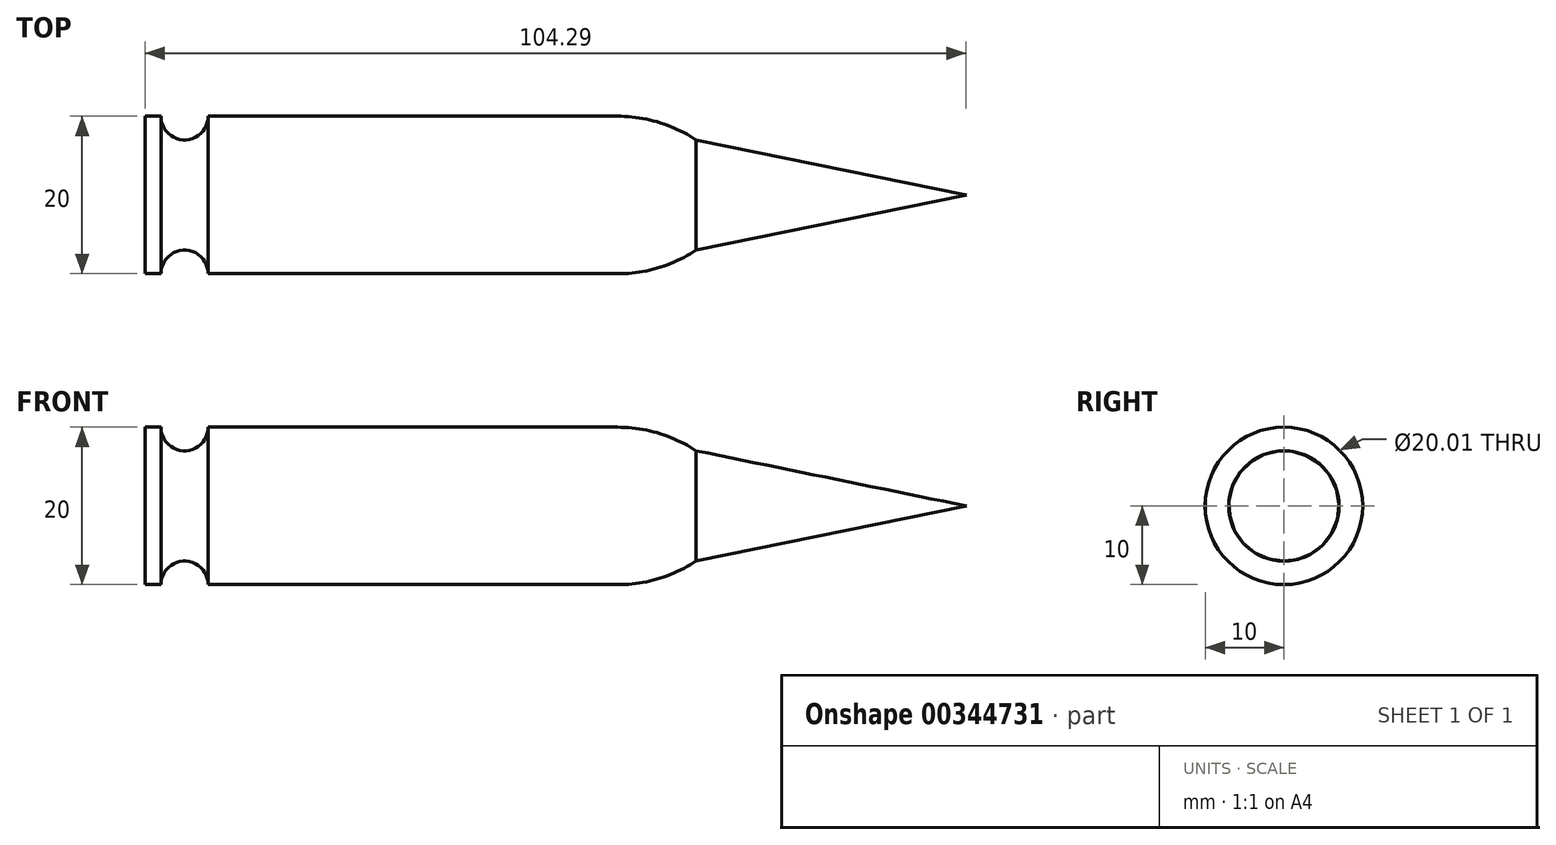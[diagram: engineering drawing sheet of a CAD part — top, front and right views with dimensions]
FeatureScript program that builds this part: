
annotation { "Feature Type Name" : "Feature", "Feature Type Description" : "" }
export const myFeature = defineFeature(function(context is Context, id is Id, definition is map)
    precondition{}
    {
        {
            var Q0;
            Q0=qCreatedBy(makeId("Front.planeOp"),FACE);
            var sketch = newSketch(context, id + "F0", { "sketchPlane" : qUnion([Q0])});
            skPoint(sketch, "E0", {"position": v(0, 10) * mm});
            skLineSegment(sketch, "E1", {"start": v(0, 10) * mm, "end": v(2, 10) * mm});
            skPoint(sketch, "E2", {"position": v(2, 10) * mm});
            skPoint(sketch, "E3", {"position": v(8, 10) * mm});
            skPoint(sketch, "E4", {"position": v(5.08, 7) * mm});
            skPoint(sketch, "E5", {"position": v(5, 10) * mm});
            skArc(sketch, "E6", {"start": v(2, 10) * mm, "mid": v(5, 7) * mm, "end": v(8, 10) * mm});
            skLineSegment(sketch, "E7.trimOffspring", {"start": v(8, 10) * mm, "end": v(10, 10) * mm});
            skPoint(sketch, "E8", {"position": v(60, 10) * mm});
            skLineSegment(sketch, "E9", {"start": v(10, 10) * mm, "end": v(60, 10) * mm});
            skPoint(sketch, "E10", {"position": v(70, 10) * mm});
            skPoint(sketch, "E11", {"position": v(70, 7) * mm});
            skArc(sketch, "E12", {"start": v(70, 7) * mm, "mid": v(65.22, 9.24) * mm, "end": v(60, 10) * mm});
            skPoint(sketch, "E13", {"position": v(104.3, 0) * mm});
            skLineSegment(sketch, "E14", {"start": v(70, 7) * mm, "end": v(104.3, 0) * mm});
            skLineSegment(sketch, "E15", {"start": v(0, 10) * mm, "end": v(0, 0) * mm});
            skSolve(sketch);
        }
        {
            var Q0;
            Q0=qCreatedBy(makeId("Front.planeOp"),FACE);
            var sketch = newSketch(context, id + "F1", { "sketchPlane" : qUnion([Q0])});
            skLineSegment(sketch, "E16", {"start": v(-16.84, 0) * mm, "end": v(-11.47, 0) * mm});
            skSolve(sketch);
        }
        {
            var Q0;
            Q0 = qConstructionFilter(qBodyType(qCreatedBy(id + "F0" ,EDGE), BodyType.WIRE), ConstructionObject.NO);
            var Q1;
            Q1=sQuery(id+"F1.wireOp",EDGE,"E16");
            revolve(context, id + "F2", {"bodyType" : ToolBodyType.SURFACE, "surfaceEntities" : qUnion([Q0]), "axis" : qUnion([Q1]), "revolveType" : RevolveType.FULL});
        }
    });
